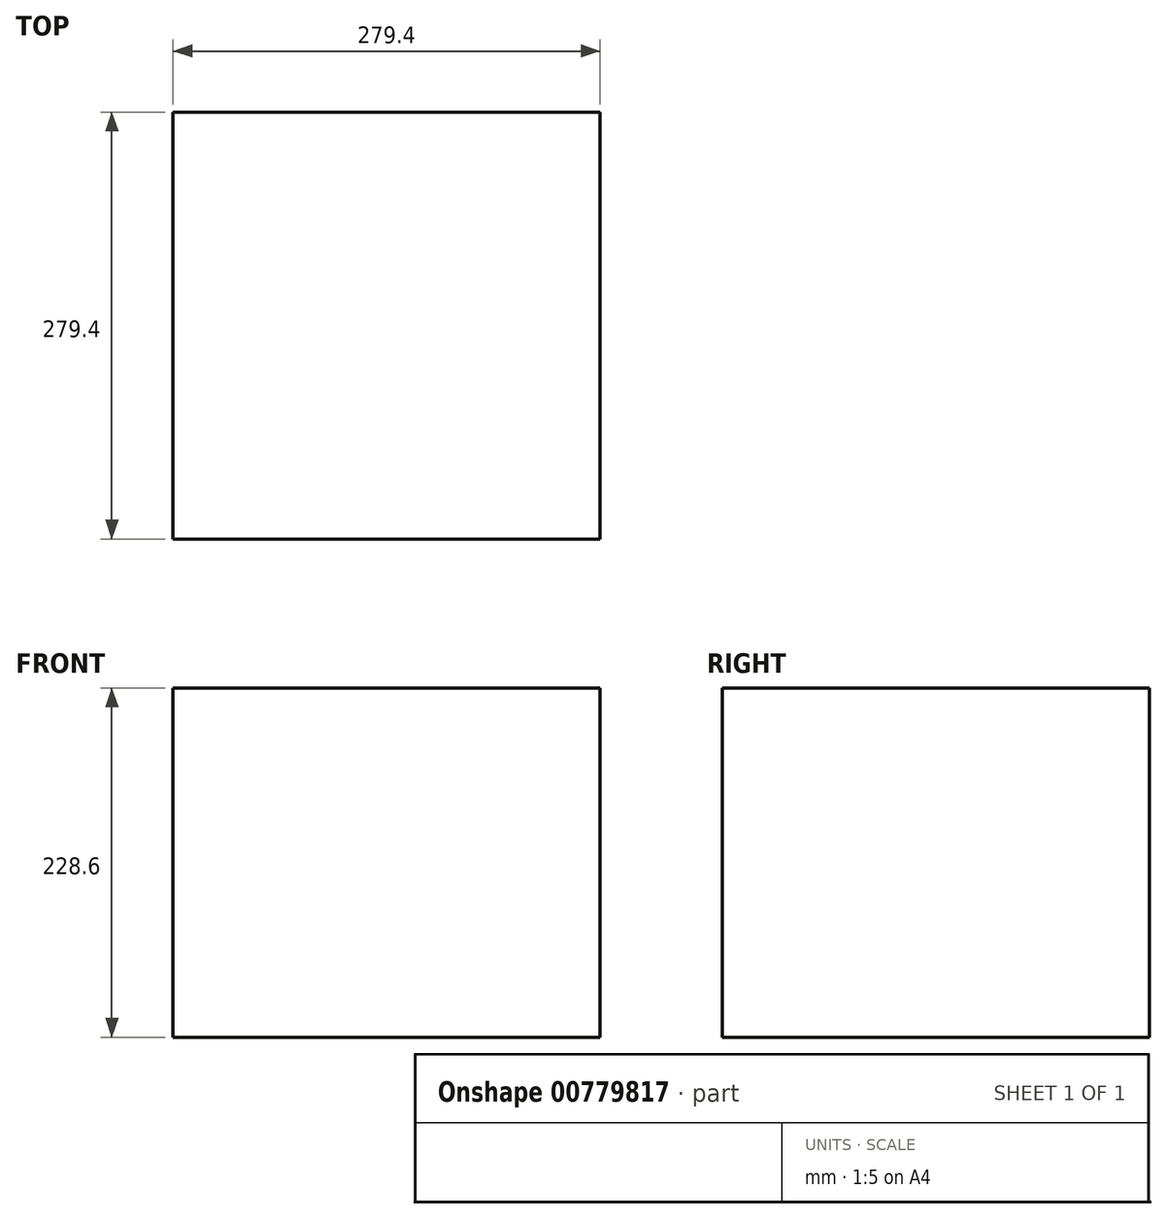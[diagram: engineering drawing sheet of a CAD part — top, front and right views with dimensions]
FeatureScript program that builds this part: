
annotation { "Feature Type Name" : "Feature", "Feature Type Description" : "" }
export const myFeature = defineFeature(function(context is Context, id is Id, definition is map)
    precondition{}
    {
        {
            var Q0;
            Q0=qCreatedBy(makeId("Top.planeOp"),FACE);
            var sketch = newSketch(context, id + "F0", { "sketchPlane" : qUnion([Q0])});
            skLineSegment(sketch, "E0.bottom", {"start": v(139.7, -139.7) * mm, "end": v(-139.7, -139.7) * mm});
            skLineSegment(sketch, "E0.top", {"start": v(139.7, 139.7) * mm, "end": v(-139.7, 139.7) * mm});
            skLineSegment(sketch, "E0.left", {"start": v(139.7, -139.7) * mm, "end": v(139.7, 139.7) * mm});
            skLineSegment(sketch, "E0.right", {"start": v(-139.7, -139.7) * mm, "end": v(-139.7, 139.7) * mm});
            skPoint(sketch, "E0.middle", {"position": v(0, 0) * mm});
            skSolve(sketch);
        }
        {
            var Q0;
            Q0=makeQuery(id+"F0.imprint","IMPRINT",FACE,{"disambiguationData":[TD([[makeQuery(id+"F0.imprint","IMPRINT",EDGE,{"derivedFrom":sQuery(id+"F0.wireOp",EDGE,"E0.bottom")}),-1.0]])]});
            extrude(context, id + "F1", {"entities" : qUnion([Q0]), "depth" : 228.6 * mm, "offsetDistance" : 25.4 * mm});
        }
    });
